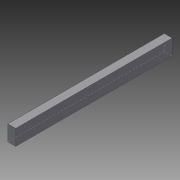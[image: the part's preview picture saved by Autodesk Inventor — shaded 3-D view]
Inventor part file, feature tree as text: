
AUTODESK INVENTOR PART (.ipt)
format: ipt  version: 2016 (Build 200138000, 138)  size: 70,656 bytes
history: native  units: mm
features: extrude x1, sketch x1
ambient origin geometry x8: Origin, YZ Plane, XZ Plane, XY Plane, X Axis, Y Axis, Z Axis, Center Point
bodies: 实体1 (feature_tree)
feature tree (2):
  extrude  "拉伸1"  Depth=40.0mm
  sketch  "草图1"  dims[d0=20.0mm d1=40.0mm d2=300.0mm d3=0.0mm]
